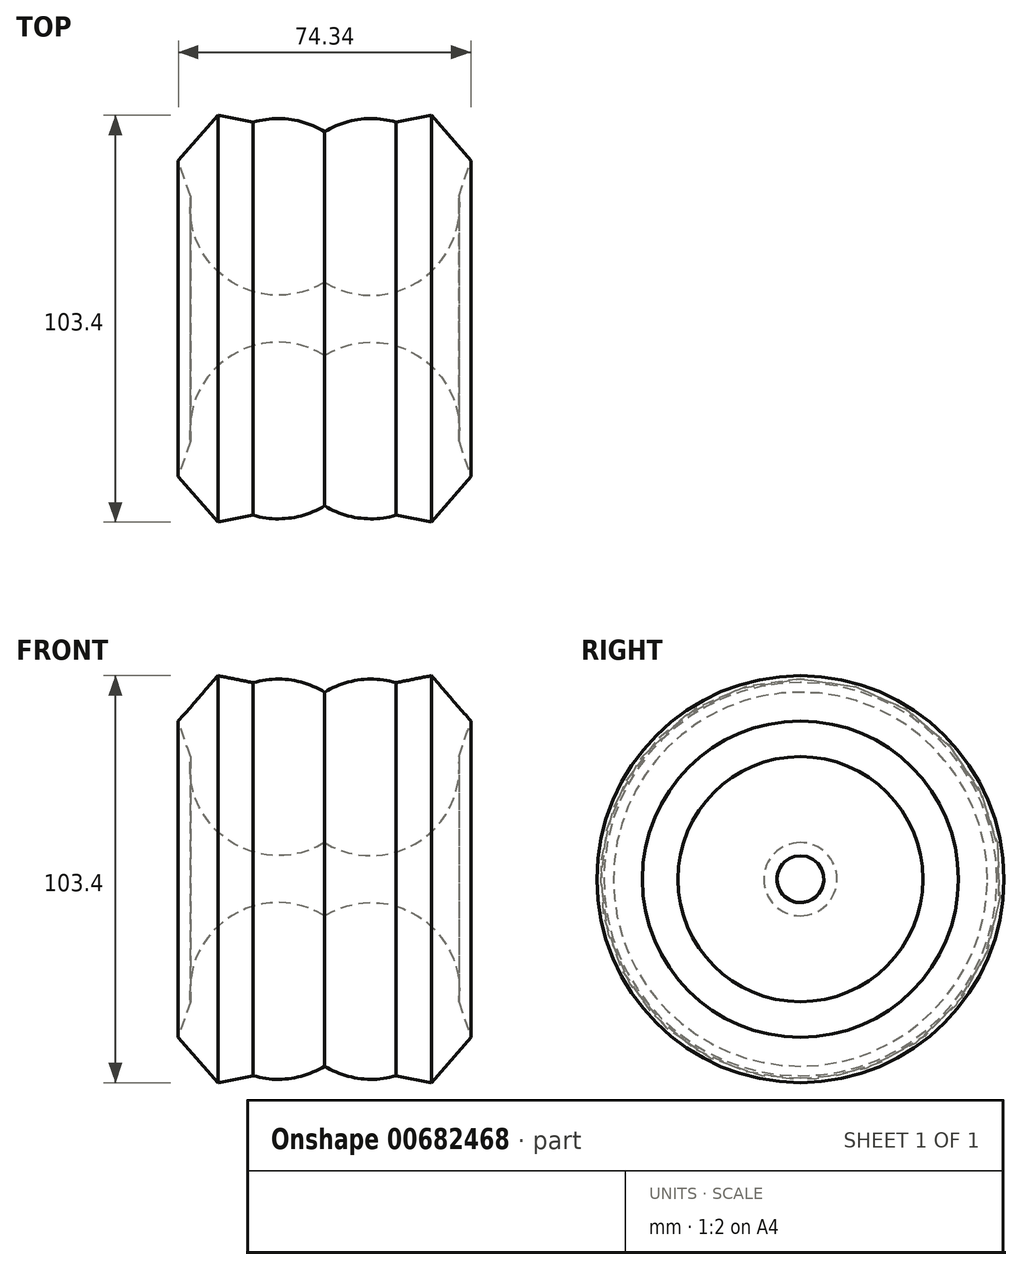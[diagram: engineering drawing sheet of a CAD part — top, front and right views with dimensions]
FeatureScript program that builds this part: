
annotation { "Feature Type Name" : "Feature", "Feature Type Description" : "" }
export const myFeature = defineFeature(function(context is Context, id is Id, definition is map)
    precondition{}
    {
        {
            var Q0;
            Q0=qCreatedBy(makeId("Front.planeOp"),FACE);
            var sketch = newSketch(context, id + "F0", { "sketchPlane" : qUnion([Q0])});
            skArc(sketch, "E0", {"start": v(-6.84, 40.9) * mm, "mid": v(-16.15, 27.03) * mm, "end": v(-5.53, 14.14) * mm});
            skArc(sketch, "E1", {"start": v(-5.53, 14.14) * mm, "mid": v(20.76, 7.82) * mm, "end": v(34.05, 31.38) * mm});
            skLineSegment(sketch, "E2.0", {"start": v(27.12, 51.7) * mm, "end": v(37.17, 40.16) * mm});
            skLineSegment(sketch, "E2.1", {"start": v(37.17, 40.16) * mm, "end": v(34.08, 31.14) * mm});
            skLineSegment(sketch, "E2.5", {"start": v(18.13, 49.94) * mm, "end": v(27.12, 51.7) * mm});
            skPoint(sketch, "E2.0.midPoint", {"position": v(32.15, 45.93) * mm});
            skPoint(sketch, "E3.orphan", {"position": v(12.1, 48.76) * mm});
            skArc(sketch, "E4.trimOffspring", {"start": v(34.05, 31.38) * mm, "mid": v(32.24, 45.82) * mm, "end": v(18.28, 49.9) * mm, "construction": true});
            skPoint(sketch, "E5.orphan", {"position": v(32.2, 25.69) * mm});
            skArc(sketch, "E6.trimOffspring", {"start": v(18.28, 49.9) * mm, "mid": v(4.24, 49.54) * mm, "end": v(-6.84, 40.9) * mm});
            skLineSegment(sketch, "E7", {"start": v(-31.65, 0) * mm, "end": v(23.5, 0) * mm});
            skSolve(sketch);
        }
        {
            var Q0;
            {var subQ2=sQuery(id+"F0.wireOp",EDGE,"E0");Q0=makeQuery(id+"F0.imprint","IMPRINT",FACE,{"disambiguationData":[TD([[makeQuery(id+"F0.imprint","IMPRINT",EDGE,{"derivedFrom":subQ2}),1.0]])]});}
            var Q1;
            Q1=sQuery(id+"F0.wireOp",EDGE,"E7");
            revolve(context, id + "F1", {"entities" : qUnion([Q0]), "axis" : qUnion([Q1]), "revolveType" : RevolveType.FULL});
        }
        {
            var Q0;
            Q0=makeQuery(id+"F1.opRevolve","SWEPT_BODY",BODY,{"disambiguationData":[OSD([sQuery(id+"F0.wireOp",EDGE,"E0"),sQuery(id+"F0.wireOp",EDGE,"E1"),sQuery(id+"F0.wireOp",EDGE,"E2.0"),sQuery(id+"F0.wireOp",EDGE,"E2.1"),sQuery(id+"F0.wireOp",EDGE,"E2.5"),sQuery(id+"F0.wireOp",EDGE,"E6.trimOffspring")])]});
            var Q1;
            Q1=qCreatedBy(makeId("Right.planeOp"),FACE);
            mirror(context, id + "F2", {"operationType" : NewBodyOperationType.ADD, "entities" : qUnion([Q0]), "mirrorPlane" : qUnion([Q1])});
        }
    });
